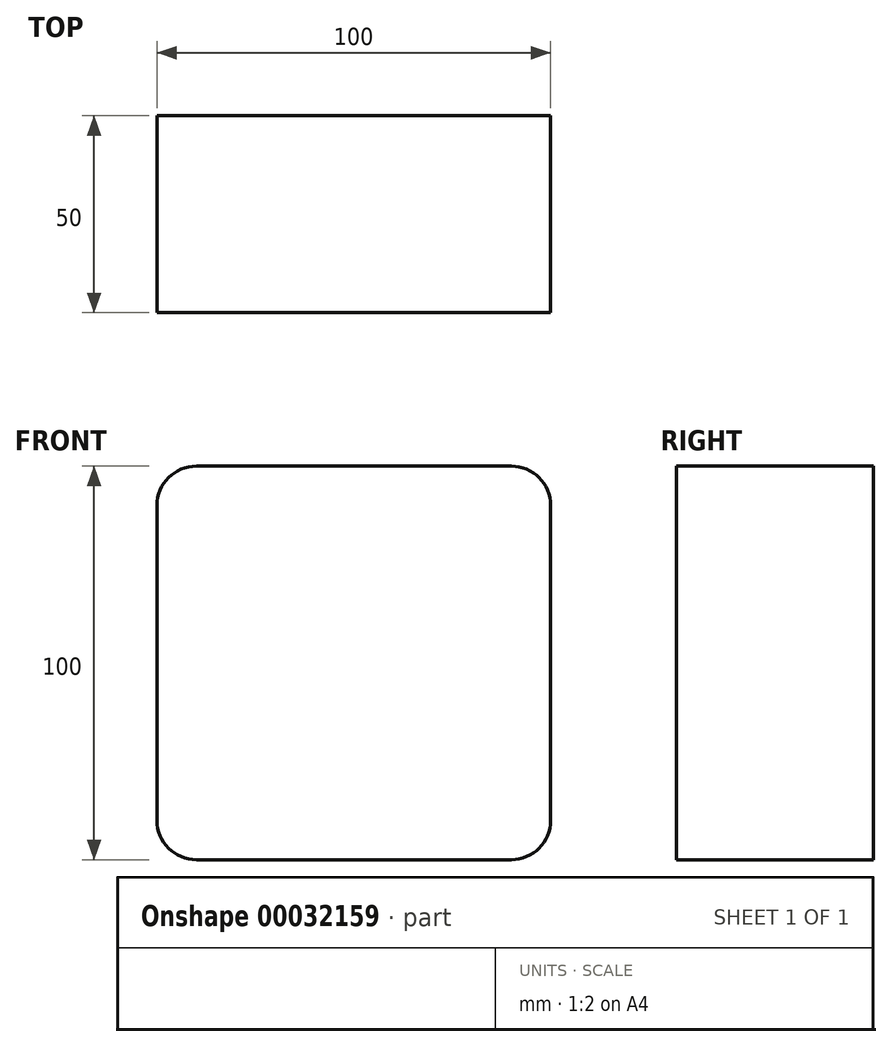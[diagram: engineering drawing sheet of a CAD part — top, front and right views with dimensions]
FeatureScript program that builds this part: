
annotation { "Feature Type Name" : "Feature", "Feature Type Description" : "" }
export const myFeature = defineFeature(function(context is Context, id is Id, definition is map)
    precondition{}
    {
        {
            var Q0;
            Q0=qCreatedBy(makeId("Front.planeOp"),FACE);
            var sketch = newSketch(context, id + "F0", { "sketchPlane" : qUnion([Q0])});
            skLineSegment(sketch, "E0.rect.bottom", {"start": v(50, 50) * mm, "end": v(-50, 50) * mm});
            skLineSegment(sketch, "E0.rect.top", {"start": v(50, -50) * mm, "end": v(-50, -50) * mm});
            skLineSegment(sketch, "E0.rect.left", {"start": v(50, 50) * mm, "end": v(50, -50) * mm});
            skLineSegment(sketch, "E0.rect.right", {"start": v(-50, 50) * mm, "end": v(-50, -50) * mm});
            skPoint(sketch, "E0.rect.middle", {"position": v(0, 0) * mm});
            skSolve(sketch);
        }
        {
            var Q0;
            Q0=makeQuery(id+"F0.imprint","IMPRINT",FACE,{"disambiguationData":[TD([[makeQuery(id+"F0.imprint","IMPRINT",EDGE,{"derivedFrom":sQuery(id+"F0.wireOp",EDGE,"E0.rect.bottom")}),1.0]])]});
            extrude(context, id + "F1", {"entities" : qUnion([Q0]), "depth" : 50 * mm});
        }
        {
            var Q0;
            Q0=makeQuery(id+"F1.opExtrude","SWEPT_EDGE",EDGE,{"disambiguationData":[OSD([sQuery(id+"F0.wireOp",EDGE,"E0.rect.bottom"),sQuery(id+"F0.wireOp",EDGE,"E0.rect.right")])]});
            var Q1;
            Q1=makeQuery(id+"F1.opExtrude","SWEPT_EDGE",EDGE,{"disambiguationData":[OSD([sQuery(id+"F0.wireOp",EDGE,"E0.rect.bottom"),sQuery(id+"F0.wireOp",EDGE,"E0.rect.left")])]});
            var Q2;
            Q2=makeQuery(id+"F1.opExtrude","SWEPT_EDGE",EDGE,{"disambiguationData":[OSD([sQuery(id+"F0.wireOp",EDGE,"E0.rect.top"),sQuery(id+"F0.wireOp",EDGE,"E0.rect.left")])]});
            var Q3;
            Q3=makeQuery(id+"F1.opExtrude","SWEPT_EDGE",EDGE,{"disambiguationData":[OSD([sQuery(id+"F0.wireOp",EDGE,"E0.rect.top"),sQuery(id+"F0.wireOp",EDGE,"E0.rect.right")])]});
            fillet(context, id + "F2", {"entities" : qUnion([Q0, Q1, Q2, Q3]), "radius" : 10 * mm, "tangentPropagation" : true, "allowEdgeOverflow" : false});
        }
    });
